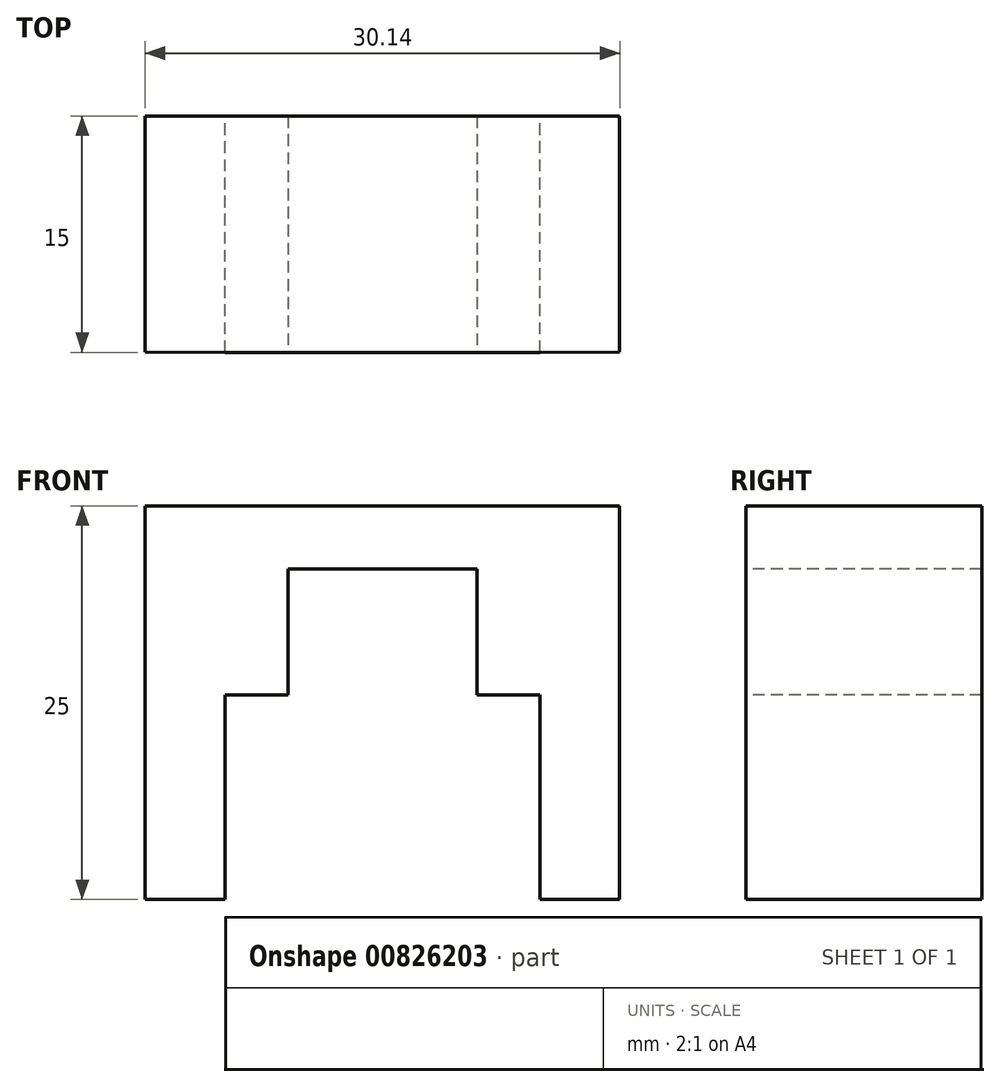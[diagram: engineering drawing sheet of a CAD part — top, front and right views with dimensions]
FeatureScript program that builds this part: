
annotation { "Feature Type Name" : "Feature", "Feature Type Description" : "" }
export const myFeature = defineFeature(function(context is Context, id is Id, definition is map)
    precondition{}
    {
        {
            var Q0;
            Q0=qCreatedBy(makeId("Top.planeOp"),FACE);
            var sketch = newSketch(context, id + "F0", { "sketchPlane" : qUnion([Q0])});
            skLineSegment(sketch, "E0.bottom", {"start": v(10, -7.5) * mm, "end": v(-10, -7.5) * mm});
            skLineSegment(sketch, "E0.top", {"start": v(10, 7.5) * mm, "end": v(-10, 7.5) * mm});
            skLineSegment(sketch, "E0.left", {"start": v(10, -7.5) * mm, "end": v(10, 7.5) * mm});
            skLineSegment(sketch, "E0.right", {"start": v(-10, -7.5) * mm, "end": v(-10, 7.5) * mm});
            skPoint(sketch, "E0.middle", {"position": v(0, 0) * mm});
            skLineSegment(sketch, "E1", {"start": v(0, 7.5) * mm, "end": v(0, -7.5) * mm, "construction": true});
            skLineSegment(sketch, "E2", {"start": v(6, 7.5) * mm, "end": v(6, -7.5) * mm});
            skLineSegment(sketch, "E3.MirrorCS", {"start": v(-6, 7.5) * mm, "end": v(-6, -7.5) * mm});
            skSolve(sketch);
        }
        {
            var Q0;
            {var subQ0=sQuery(id+"F0.wireOp",EDGE,"E0.right");Q0=makeQuery(id+"F0.imprint","IMPRINT",FACE,{"disambiguationData":[TD([[makeQuery(id+"F0.imprint","IMPRINT",EDGE,{"derivedFrom":subQ0}),-1.0]])]});}
            var Q1;
            {var subQ0=sQuery(id+"F0.wireOp",EDGE,"E2");Q1=makeQuery(id+"F0.imprint","IMPRINT",FACE,{"disambiguationData":[TD([[makeQuery(id+"F0.imprint","IMPRINT",EDGE,{"derivedFrom":subQ0}),-1.0]])]});}
            var Q2;
            {var subQ0=sQuery(id+"F0.wireOp",EDGE,"E0.left");Q2=makeQuery(id+"F0.imprint","IMPRINT",FACE,{"disambiguationData":[TD([[makeQuery(id+"F0.imprint","IMPRINT",EDGE,{"derivedFrom":subQ0}),1.0]])]});}
            extrude(context, id + "F1", {"entities" : qUnion([Q0, Q1, Q2]), "depth" : 12 * mm, "offsetDistance" : 25 * mm});
        }
        {
            var Q0;
            {var subQ0=sQuery(id+"F0.wireOp",EDGE,"E2");Q0=makeQuery(id+"F0.imprint","IMPRINT",FACE,{"disambiguationData":[TD([[makeQuery(id+"F0.imprint","IMPRINT",EDGE,{"derivedFrom":subQ0}),-1.0]])]});}
            extrude(context, id + "F2", {"entities" : qUnion([Q0]), "operationType" : NewBodyOperationType.REMOVE, "depth" : 8 * mm, "offsetDistance" : 25 * mm});
        }
        {
            var Q0;
            Q0=makeQuery(id+"F1.opExtrude","CAP_FACE",FACE,{"disambiguationData":[OSD([sQuery(id+"F0.wireOp",EDGE,"E0.bottom"),sQuery(id+"F0.wireOp",EDGE,"E0.top"),sQuery(id+"F0.wireOp",EDGE,"E0.left"),sQuery(id+"F0.wireOp",EDGE,"E0.right")])],"isStart":false});
            var sketch = newSketch(context, id + "F3", { "sketchPlane" : qUnion([Q0])});
            skLineSegment(sketch, "E4", {"start": v(10, 7.5) * mm, "end": v(15.07, 7.5) * mm});
            skLineSegment(sketch, "E5", {"start": v(15.07, 7.5) * mm, "end": v(15.07, -7.49) * mm});
            skLineSegment(sketch, "E6", {"start": v(15.07, -7.49) * mm, "end": v(10, -7.5) * mm});
            skLineSegment(sketch, "E7.MirrorCS", {"start": v(-10, 7.5) * mm, "end": v(-15.07, 7.5) * mm});
            skLineSegment(sketch, "E8.MirrorCS", {"start": v(-15.07, 7.5) * mm, "end": v(-15.07, -7.49) * mm});
            skLineSegment(sketch, "E9.MirrorCS", {"start": v(-15.07, -7.49) * mm, "end": v(-10, -7.5) * mm});
            skSolve(sketch);
        }
        {
            var Q0;
            Q0=makeQuery(id+"F3.imprint","IMPRINT",FACE,{"disambiguationData":[TD([[makeQuery(id+"F3.imprint","IMPRINT",EDGE,{"derivedFrom":sQuery(id+"F3.wireOp",EDGE,"E7.MirrorCS")}),1.0]])]});
            var Q1;
            Q1=makeQuery(id+"F3.imprint","IMPRINT",FACE,{"disambiguationData":[TD([[makeQuery(id+"F3.imprint","IMPRINT",EDGE,{"derivedFrom":sQuery(id+"F3.wireOp",EDGE,"E4")}),-1.0]])]});
            extrude(context, id + "F4", {"entities" : qUnion([Q0, Q1]), "operationType" : NewBodyOperationType.ADD, "oppositeDirection" : true, "depth" : 25 * mm, "offsetDistance" : 25 * mm});
        }
    });
